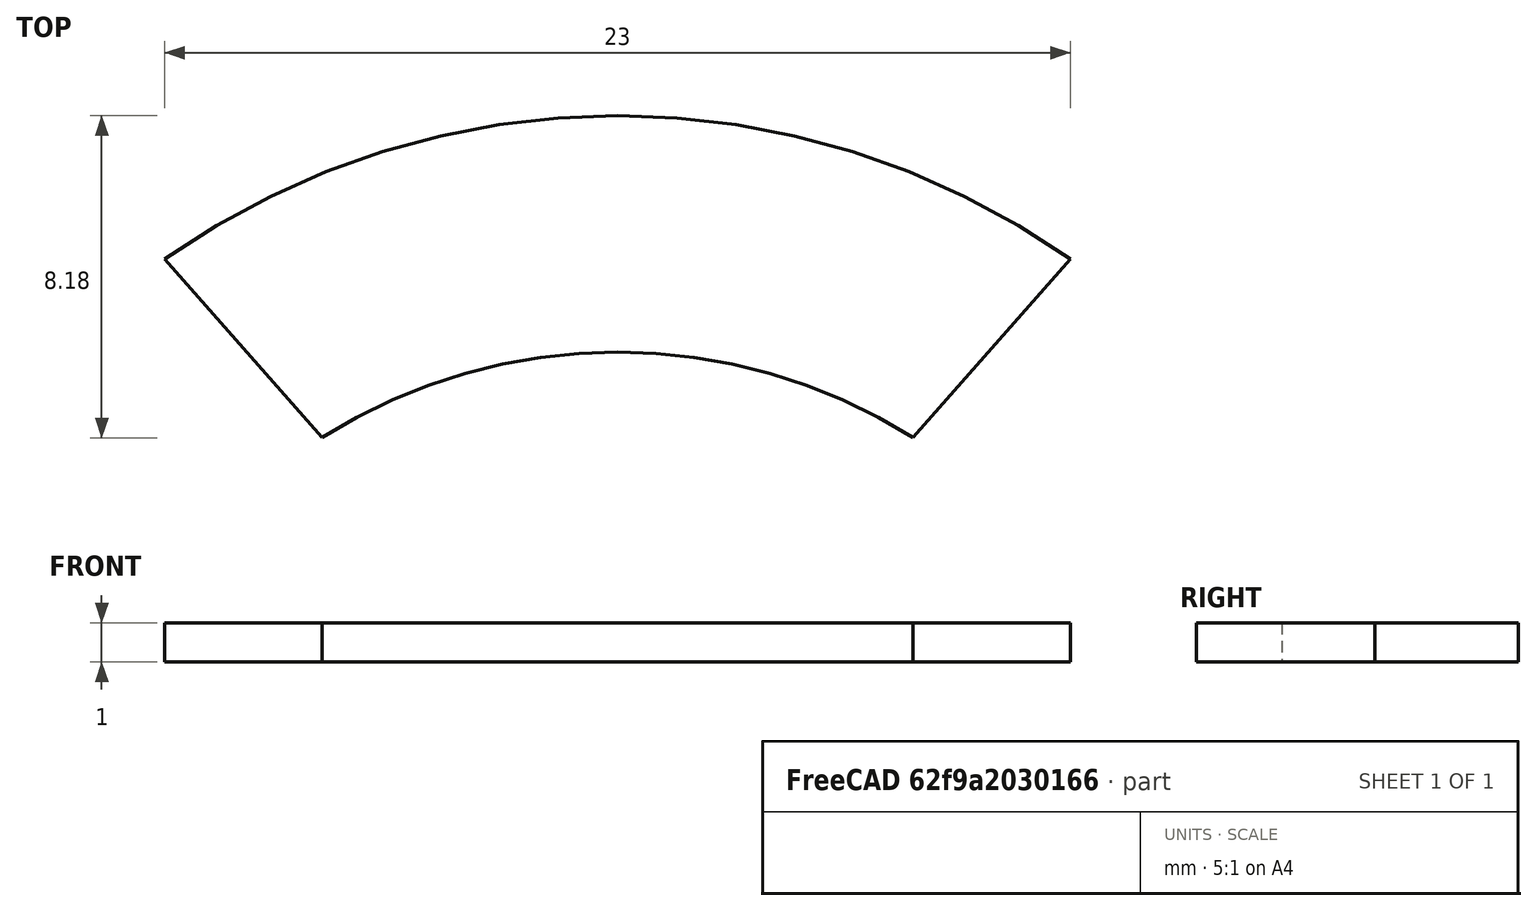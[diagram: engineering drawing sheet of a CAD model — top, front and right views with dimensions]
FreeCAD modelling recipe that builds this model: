
FCSTD DOCUMENT  (FreeCAD 0.21R33771 (Git))
Label: dipole
License: All rights reserved
LicenseURL: https://en.wikipedia.org/wiki/All_rights_reserved
objects: Sketcher::SketchObject×1, TechDraw::DrawSVGTemplate×1, PartDesign::Pad×1, PartDesign::Body×1, TechDraw::DrawViewPart×1, TechDraw::DrawPage×1
note: 4 computed .brp shape members not serialized (recipe doc carries the construction recipe); baked Part::Feature solids carry a one-line shape summary decoded from their .brp

FEATURE [Sketcher::SketchObject] Sketch
  FullyConstrained = false
  sketch-geometry (9):
    g0: ArcOfCircle CenterX=0 CenterY=0 CenterZ=0 NormalX=0 NormalY=0 NormalZ=1 AngleXU=0 Radius=20 StartAngle=0.958192 EndAngle=2.1834
    g1: ArcOfCircle CenterX=0 CenterY=0 CenterZ=0 NormalX=0 NormalY=0 NormalZ=1 AngleXU=0 Radius=14 StartAngle=1.00544 EndAngle=2.13615
    g2: LineSegment StartX=-11.5 StartY=16.3631 StartZ=0 EndX=-7.5 EndY=11.8216 EndZ=0
    g3: LineSegment StartX=7.5 StartY=11.8216 StartZ=0 EndX=11.5 EndY=16.3631 EndZ=0
    g4: LineSegment StartX=-11.5 StartY=16.3631 StartZ=0 EndX=-11.5 EndY=11.8216 EndZ=0
    g5: LineSegment StartX=-11.5 StartY=11.8216 StartZ=0 EndX=-7.5 EndY=11.8216 EndZ=0
    g6: LineSegment StartX=7.5 StartY=11.8216 StartZ=0 EndX=11.5 EndY=11.8216 EndZ=0
    g7: LineSegment StartX=11.5 StartY=11.8216 StartZ=0 EndX=11.5 EndY=16.3631 EndZ=0
    g8: GeomPoint X=0.895372 Y=21.9774 Z=0
  constraints (22):
    c: Coincident(g0,g-1)
    c: Radius(g0) = 20
    c: Coincident(g1,g0)
    c: Radius(g1) = 14
    c: Coincident(g2,g0)
    c: Coincident(g2,g1)
    c: Coincident(g3,g1)
    c: Coincident(g3,g0)
    c: DistanceX(g1,g1) = 15
    c: DistanceX(g0,g0) = 23
    c: Coincident(g4,g0)
    c: Vertical(g4)
    c: Coincident(g5,g4)
    c: Coincident(g5,g1)
    c: Coincident(g6,g1)
    c: Horizontal(g6)
    c: Coincident(g7,g6)
    c: Coincident(g7,g0)
    c: Angle(g6,g7,g6) = 1.5708
    c: Angle(g4,g5,g4) = 1.5708
    c: Equal(g6,g5)
    c: Equal(g3,g2)
FEATURE [TechDraw::DrawSVGTemplate] Template
  EditableTexts = Designed_by_Name=Designed by Name; Drawing_number=Drawing number; FC-Date=Date; FC-SC=Scale; FC-SH=Sheet; FC-Title=Title; Subtitle=Subtitle; Weight=Weight
  Height = 210
  Orientation = 1
  Template = <path>
  Width = 297
FEATURE [PartDesign::Pad] Pad
  Direction = (0,0,1)
  Length = 1
  Length2 = 10
  Profile = -> Sketch
  ReferenceAxis = -> Sketch [N_Axis]
  Type = 0
FEATURE [PartDesign::Body] Body
  Group = -> [Sketch,Pad]
  Origin = -> Origin
  Tip = -> Pad
FEATURE [TechDraw::DrawViewPart] View
  CoarseView = false
  Direction = (0,0,1)
  Focus = 100
  HardHidden = false
  IsoCount = 0
  IsoHidden = false
  IsoVisible = false
  LockPosition = false
  Perspective = false
  Rotation = 0
  Scale = 10
  ScaleType = 0
  ScrubCount = 0
  SeamHidden = false
  SeamVisible = false
  SmoothHidden = false
  SmoothVisible = true
  Source = -> [Body]
  X = 153.2
  XDirection = (1,0,0)
  Y = 129.024
FEATURE [TechDraw::DrawPage] Page
  KeepUpdated = true
  NextBalloonIndex = 1
  ProjectionType = 0
  Scale = 10
  Template = -> Template
  Views = -> [View]
note: 1 file-system path scrubbed to <path> (originals preserved in the JSON sidecar)
